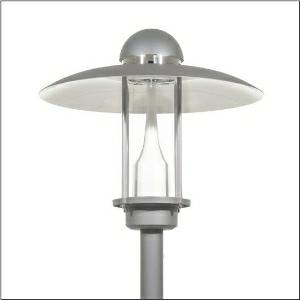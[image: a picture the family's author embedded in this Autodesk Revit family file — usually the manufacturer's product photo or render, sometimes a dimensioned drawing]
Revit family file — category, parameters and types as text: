
# Revit family: city-light_elegance_iq___st1_2a_5xa5265ef14h_e69b
name_source: partatom
category: Lighting Fixtures
units: mm (PartAtom-declared; Revit-internal decimal feet)

## family parameters
Cut with Voids When Loaded = No
Host = Face
Light Source = No
Part Type = Normal
Room Calculation Point = No
Round Connector Dimension = Use Diameter
Shared = No

## types (1)
- --- (1 x LED, 1470 lm, 10.5 W, 3000K)
    Apparent Load = 11 VA
    CIE Flux Codes = 22 62 94 98 100
    Color Rendering = 70
    Color Temperature = 3000K
    Default Elevation = 1800 mm
    Description = City-Light Elegance iQ, mast luminaire, Module 540 iQ-SR, primary light control with 3 zone facetted reflector, of plastic, silver coated, highly specular, structured, primary optical cover: cover, of PMMA, transparent, light distribution: ST1.2a, light emission: direct distribution, primary light characteristic: asymmetric, installation type: post-top, LED, High Power LED, rated luminous flux: 1.470lm, luminous efficacy: 140lm/W, light colour: 730, colour temperature: 3000K, control gear: iQ Street-Remote, control: Auto-Match, Temp-Guard, Lumen-Switch, Night-Set, Smart-Wire, Light-Fading, Desk-Remote (wireless, voltage-free reading and setting of iQ features in the workshop via application-optimized NFC function/RFID function), optimised constant luminous flux control (CLO 2.0), Street-Remote, pre-setting: logarithmic dimming characteristic, with terminal, 6-pole, max. 2.5mm², mains connection: 230..240V, AC, 50/60Hz, start of lifetime: 11W, end of service life: 11W, reduction: 5W, luminaire housing, upper part, of aluminium, coated, Siteco® metallic grey (DB 702S), diameter: 750mm, height: 675mm, spigot size: d x l = 76 x 70mm (post-top) | with reducer (optional accessory) 60 x 70mm, mounting height: 3..5m, post-top mast mounting element, of diecast aluminium, coated, Siteco® metallic grey (DB 702S), Module 540 iQ-SR, traffic white (RAL 9016), equipment: standard, protection rating (complete): IP65, insulation class (complete): insulation class II (safety insulation), certification: CE, ENEC, VDE, packaging unit: 1 piece

Light Distribution: ST1.2a
    Height = 675 mm
    Lamp = 1 x LED
    Lamp Light Flux = 1470 lm
    Lamp Power = 10.5 W
    Lamp count = 1
    Length = 750 mm
    Luminous efficacy = 140 lm/W
    Manufacturer = Siteco
    ModVariant = No
    Model = 5XA5265EF14H
    Number of Poles = 1
    OnlyDefault = Yes
    Power Factor = 1
    Product Name = City-Light Elegance iQ | ST1.2a
    Product group = mast luminaire | pylon top
    ProductGroupID = 6100
    Protection Class = Protection class II
    Protection Degree = IP 65
    RLX_Detail_Level = 1
    RLX_Emergency_Light_Flux = 0 lm
    RLX_Emergency_Type = 0
    RLX_Emergency_Type_DB = No
    RlxData = <blob elided: 99921 chars, md5=cf441e92>
    Socket = socket
    Standby Power = 0 W
    System Light Flux = 1470 lm
    System Power = 11 W
    Type Comments = factory setting: luminous flux: 100 % | dim-lin: 254 | 419 mA
    Type Image = l_1006912.jpg
    URL = http://relux.com
    VarID = @adj_181321
    Voltage = 0 V
    Weight = 0.00 kg
    Width = 0 mm  [stored 0 ft]

note: [stored X ft] marks values corroborated as IEEE doubles in the binary element streams (Revit-internal decimal feet)

## geometry (parser evidence)
native form markers: Blend x4, Sweep x11
no freeform markers — native parametric forms only
